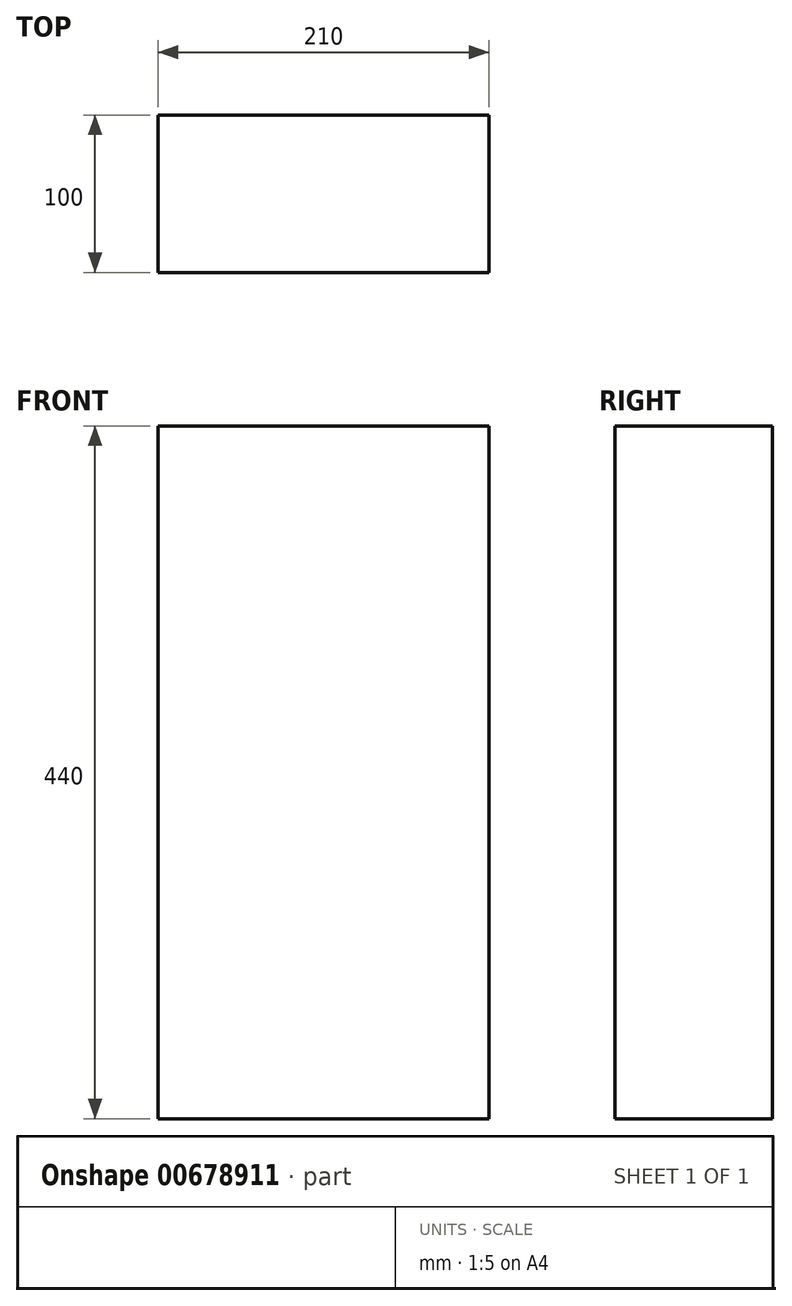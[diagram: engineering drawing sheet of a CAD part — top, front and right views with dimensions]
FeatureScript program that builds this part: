
annotation { "Feature Type Name" : "Feature", "Feature Type Description" : "" }
export const myFeature = defineFeature(function(context is Context, id is Id, definition is map)
    precondition{}
    {
        {
            var Q0;
            Q0=qCreatedBy(makeId("Front.planeOp"),FACE);
            var sketch = newSketch(context, id + "F0", { "sketchPlane" : qUnion([Q0])});
            skLineSegment(sketch, "E0.bottom", {"start": v(0, 0) * mm, "end": v(210, 0) * mm});
            skLineSegment(sketch, "E0.top", {"start": v(0, 440) * mm, "end": v(210, 440) * mm});
            skLineSegment(sketch, "E0.left", {"start": v(0, 0) * mm, "end": v(0, 440) * mm});
            skLineSegment(sketch, "E0.right", {"start": v(210, 0) * mm, "end": v(210, 440) * mm});
            skSolve(sketch);
        }
        {
            var Q0;
            Q0 = qSketchRegion(id + "F0", true);
            extrude(context, id + "F1", {"entities" : qUnion([Q0]), "depth" : 100 * mm, "offsetDistance" : 25 * mm});
        }
    });
